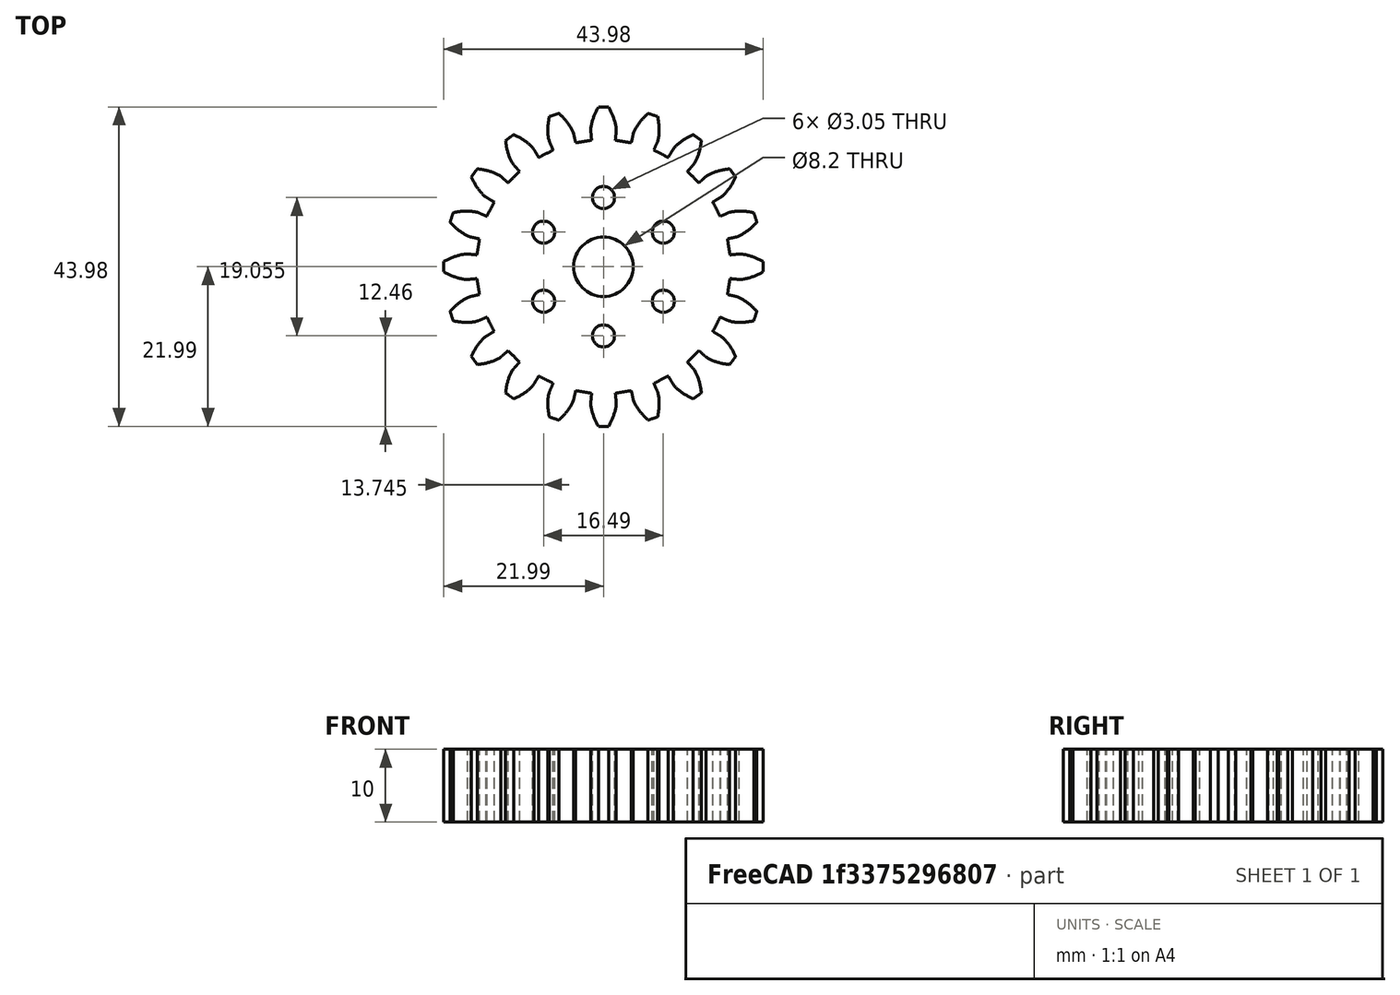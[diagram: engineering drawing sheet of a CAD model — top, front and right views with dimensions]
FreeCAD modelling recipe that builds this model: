
FCSTD DOCUMENT  (FreeCAD 0.19R17798 (Git))
Label: gear20
License: All rights reserved
LicenseURL: http://en.wikipedia.org/wiki/All_rights_reserved
objects: Part::Cylinder×7, Part::Cut×7, Part::FeaturePython×1
note: 15 computed .brp shape members not serialized (recipe doc carries the construction recipe); baked Part::Feature solids carry a one-line shape summary decoded from their .brp

FEATURE [Part::FeaturePython] InvoluteGear  # WARN: FeaturePython — macro-defined, semantics opaque (R4)
  backlash = 0
  beta = 0
  clearance = 0.25
  double_helix = false
  head = 0
  height = 10
  module = 2
  numpoints = 6
  pressure_angle = 20
  reversed_backlash = false
  shift = 0
  simple = false
  teeth = 20
  undercut = false
FEATURE [Part::Cylinder] Cylinder
  Angle = 360
  AttacherType = Attacher::AttachEngine3D
  Height = 30
  Placement = pos=(0,0,-10) rot=(0,0,1;0rad)
  Radius = 4.1
FEATURE [Part::Cylinder] Cylinder001
  Angle = 360
  AttacherType = Attacher::AttachEngine3D
  Height = 30
  Placement = pos=(8.245,4.762,-10) rot=(0,0,1;0rad)
  Radius = 1.525
FEATURE [Part::Cylinder] Cylinder002
  Angle = 360
  AttacherType = Attacher::AttachEngine3D
  Height = 30
  Placement = pos=(0,9.525,-10) rot=(0,0,1;0rad)
  Radius = 1.525
FEATURE [Part::Cylinder] Cylinder003
  Angle = 360
  AttacherType = Attacher::AttachEngine3D
  Height = 30
  Placement = pos=(-8.245,4.762,-10) rot=(0,0,1;0rad)
  Radius = 1.525
FEATURE [Part::Cylinder] Cylinder004
  Angle = 360
  AttacherType = Attacher::AttachEngine3D
  Height = 30
  Placement = pos=(-8.245,-4.762,-10) rot=(0,0,1;0rad)
  Radius = 1.525
FEATURE [Part::Cylinder] Cylinder005
  Angle = 360
  AttacherType = Attacher::AttachEngine3D
  Height = 30
  Placement = pos=(0,-9.53,-10) rot=(0,0,1;0rad)
  Radius = 1.525
FEATURE [Part::Cylinder] Cylinder006
  Angle = 360
  AttacherType = Attacher::AttachEngine3D
  Height = 30
  Placement = pos=(8.245,-4.76,-10) rot=(0,0,1;0rad)
  Radius = 1.525
FEATURE [Part::Cut] Cut
  Base = -> InvoluteGear
  Refine = true
  Tool = -> Cylinder
FEATURE [Part::Cut] Cut001
  Base = -> Cut
  Refine = true
  Tool = -> Cylinder001
FEATURE [Part::Cut] Cut002
  Base = -> Cut001
  Refine = true
  Tool = -> Cylinder002
FEATURE [Part::Cut] Cut003
  Base = -> Cut002
  Refine = true
  Tool = -> Cylinder003
FEATURE [Part::Cut] Cut004
  Base = -> Cut003
  Refine = true
  Tool = -> Cylinder004
FEATURE [Part::Cut] Cut005
  Base = -> Cut004
  Refine = true
  Tool = -> Cylinder005
FEATURE [Part::Cut] Cut006
  Base = -> Cut005
  Refine = true
  Tool = -> Cylinder006
